# Revit family: HEATER
name_source: partatom
category: Wyposażenie mechaniczne
revit_build: Autodesk Revit 2018 (Build: 20170927_1515(x64)
units: mm (PartAtom-declared; Revit-internal decimal feet)

## family parameters
Klasyfikacja = Brak
Obiekt nadrzędny = Powierzchnia
Punkt obliczania pomieszczeń = Nie
Tnij formami wycięć po wczytaniu = Nie
Typ części = Normalny
Współdzielony = Nie
Wymiar okrągłego złącza = Użyj średnicy

## types (10) — shared parameters
Autor = www.archispace.com
Domyślna rzędna = 1219 mm
Opis = Тепловентилятор
Producent = Sonninger Sp. z o.o. Sp. k.
Класс защиты = IP54
Максимальное рабочее давление = 1600000.0 Pa
Напряжение питания = 230 V
максимальная температура среды = 90 °C
материал = Body - PPT material
минимальная высота установки = 4 mm  [stored 0.0131234 ft]

## per-type parameters (varying)
| type | Model | O | PPU | Диаметры патрубков | Количество рядов нагревателя | Максимальная высота установки | Максимальный диапазон воздуха | Максимальный расход воздуха | Масса оборудования | Мощность обогрева max. | Мощность обогрева min. | Мощность электродвигателя | Уровень шума | Частота вращения двигателя | масса оборудования с водой |
| ONE - настенный монтаж | Heater One | 0 mm  [stored 0 ft] | PPU : HORIZONTAL - ONE, R1 | 13 | 2 | 9 mm  [stored 0.0295276 ft] | 14000 mm  [stored 45.9318 ft] | 1900.0 m³/h | 9.60 kg | 20 kW | 5 kW | 124 W | 54.2 | 1400 | 10.70 kg |
| R1 - настенный монтаж | Heater R1 | 0 mm  [stored 0 ft] | PPU : HORIZONTAL - ONE, R1 | 19 | 1 | 11 mm  [stored 0.0360892 ft] | 27000 mm  [stored 88.5827 ft] | 4100.0 m³/h | 10.80 kg | 30 kW | 10 kW | 250 W | 59.4 | 1350 | 11.90 kg |
| R2 - настенный монтаж | Heater R2 | 0 mm  [stored 0 ft] | PPU : HORIZONTAL - R2, SPECIAL | 19 | 2 | 11 mm  [stored 0.0360892 ft] | 25000 mm  [stored 82.021 ft] | 3500.0 m³/h | 12.70 kg | 50 kW | 30 kW | 250 W | 59.4 | 1350 | 14.80 kg |
| R3 - настенный монтаж | Heater R3 | 0 mm  [stored 0 ft] | PPU : HORIZONTAL - R3 | 19 | 3 | 11 mm  [stored 0.0360892 ft] | 24000 mm  [stored 78.7402 ft] | 3400.0 m³/h | 14.50 kg | 70 kW | 50 kW | 360 W | 60.5 | 1400 | 16.90 kg |
| SPECIAL - настенный монтаж | Heater Special | 0 mm  [stored 0 ft] | PPU : HORIZONTAL - R2, SPECIAL | 19 | 3 | 11 mm  [stored 0.0360892 ft] | 24 mm  [stored 0.0787402 ft] | 4500.0 m³/h | 14.50 kg | 45 kW | 20 kW | 250 W | 56 | 1350 | 16.90 kg |
| ONE потолочный монтаж | Heater One | 201 mm | PPU : VERTICAL - ONE | 19 | 2 | 9 mm  [stored 0.0295276 ft] | 14000 mm  [stored 45.9318 ft] | 1900.0 m³/h | 9.60 kg | 20 kW | 5 kW | 250 W | 54.2 | 1350 | 10.70 kg |
| R1 - потолочный монтаж | Heater R1 | 227 mm  [stored 0.744751 ft] | PPU : VERTICAL - R1, R2, R3, SPECIAL | 19 | 1 | 11 mm  [stored 0.0360892 ft] | 27000 mm  [stored 88.5827 ft] | 4100.0 m³/h | 10.80 kg | 30 kW | 10 kW | 250 W | 59.4 | 1350 | 11.90 kg |
| R2 - потолочный монтаж | Heater R1 | 227 mm  [stored 0.744751 ft] | PPU : VERTICAL - R1, R2, R3, SPECIAL | 19 | 1 | 11 mm  [stored 0.0360892 ft] | 25000 mm  [stored 82.021 ft] | 3500.0 m³/h | 12.70 kg | 50 kW | 30 kW | 250 W | 59.4 | 1350 | 14.80 kg |
| R3 - потолочный монтаж | Heater R1 | 227 mm  [stored 0.744751 ft] | PPU : VERTICAL - R1, R2, R3, SPECIAL | 19 | 1 | 11 mm  [stored 0.0360892 ft] | 24000 mm  [stored 78.7402 ft] | 3400.0 m³/h | 14.50 kg | 70 kW | 50 kW | 360 W | 60.5 | 1400 | 16.90 kg |
| SPECIAL - потолочный монтаж | Heater R1 | 227 mm  [stored 0.744751 ft] | PPU : VERTICAL - R1, R2, R3, SPECIAL | 19 | 1 | 11 mm  [stored 0.0360892 ft] | 27000 mm  [stored 88.5827 ft] | 4900.0 m³/h | 10.80 kg | 30 kW | 10 kW | 250 W | 56 | 1350 | 11.90 kg |

note: [stored X ft] marks values corroborated as IEEE doubles in the binary element streams (Revit-internal decimal feet)
